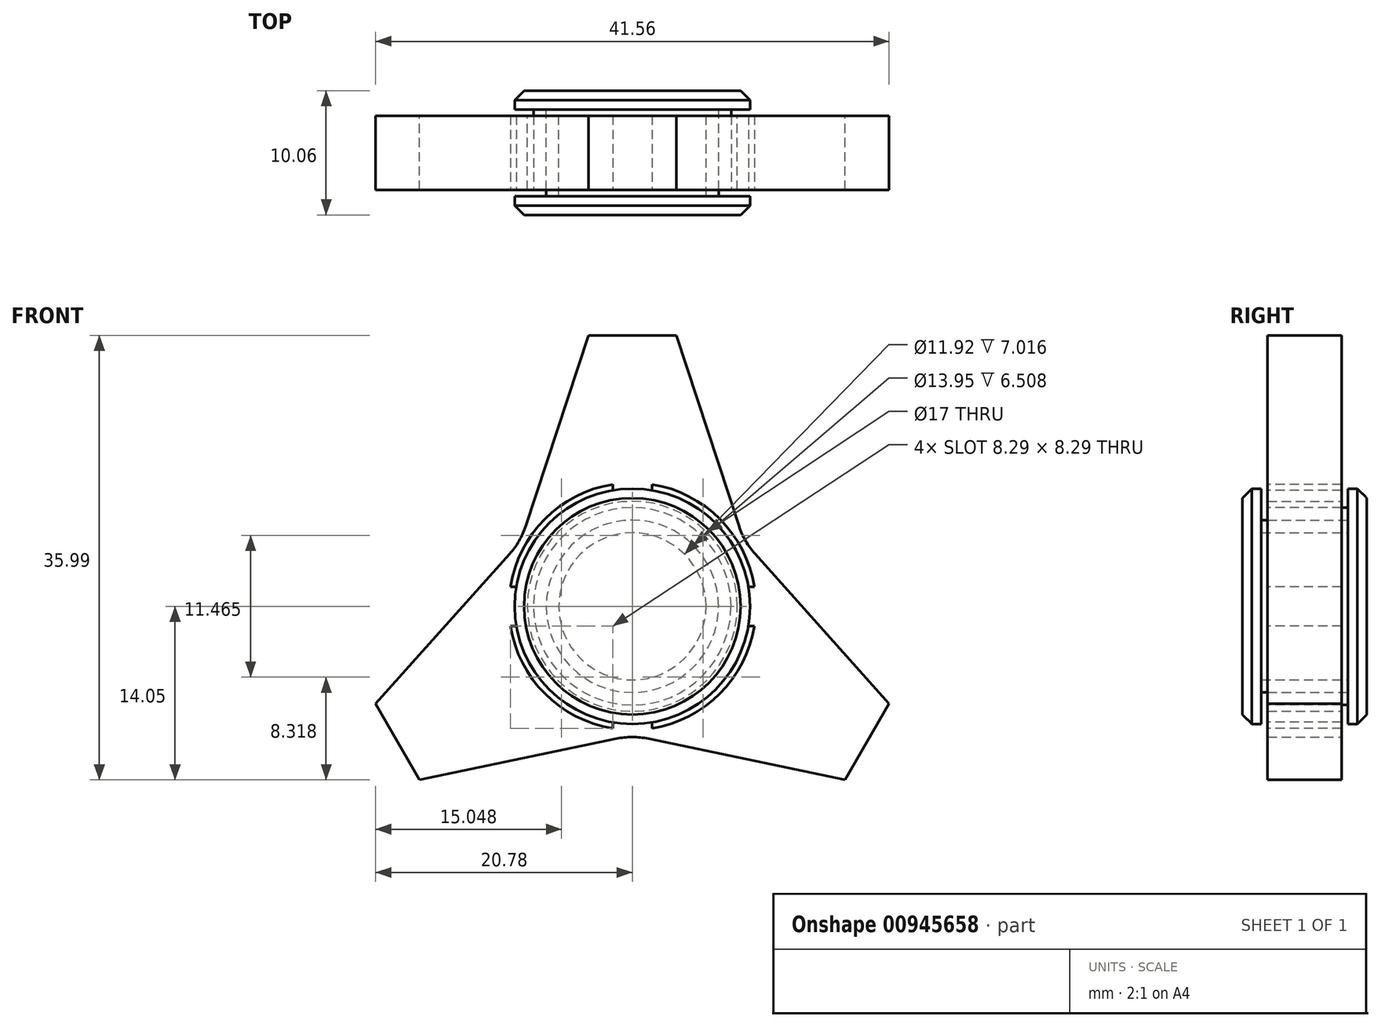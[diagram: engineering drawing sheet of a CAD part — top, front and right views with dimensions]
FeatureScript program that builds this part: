
annotation { "Feature Type Name" : "Feature", "Feature Type Description" : "" }
export const myFeature = defineFeature(function(context is Context, id is Id, definition is map)
    precondition{}
    {
        {
            var Q0;
            Q0=qCreatedBy(makeId("Front.planeOp"),FACE);
            var sketch = newSketch(context, id + "F0", { "sketchPlane" : qUnion([Q0])});
            skCircle(sketch, "E0", {"center": v(0, 0) * mm, "radius": 8.5 * mm});
            skCircle(sketch, "E1.cCircle", {"center": v(0, 0) * mm, "radius": 22.23 * mm, "construction": true});
            skPoint(sketch, "E1.0.midPoint", {"position": v(-19.31, -11) * mm});
            skLineSegment(sketch, "E2", {"start": v(-3.56, 21.94) * mm, "end": v(3.56, 21.94) * mm});
            skLineSegment(sketch, "E3", {"start": v(3.56, 21.94) * mm, "end": v(8.64, 6.49) * mm});
            skLineSegment(sketch, "E4", {"start": v(-3.56, 21.94) * mm, "end": v(-8.64, 6.49) * mm});
            skLineSegment(sketch, "E5.1.0", {"start": v(20.78, -7.89) * mm, "end": v(9.93, 4.24) * mm});
            skLineSegment(sketch, "E5.1.1", {"start": v(17.22, -14.05) * mm, "end": v(1.3, -10.72) * mm});
            skLineSegment(sketch, "E5.1.2", {"start": v(20.78, -7.89) * mm, "end": v(17.22, -14.05) * mm});
            skLineSegment(sketch, "E5.2.0", {"start": v(-17.22, -14.05) * mm, "end": v(-1.3, -10.72) * mm});
            skLineSegment(sketch, "E5.2.1", {"start": v(-20.78, -7.89) * mm, "end": v(-9.93, 4.24) * mm});
            skLineSegment(sketch, "E5.2.2", {"start": v(-17.22, -14.05) * mm, "end": v(-20.78, -7.89) * mm});
            skLineSegment(sketch, "E5.anchor1", {"start": v(0, 0) * mm, "end": v(-10.77, 0) * mm, "construction": true});
            skLineSegment(sketch, "E5.anchor2", {"start": v(0, 0) * mm, "end": v(5.38, -9.33) * mm, "construction": true});
            skPoint(sketch, "E6.orphan", {"position": v(-5.38, 9.33) * mm});
            skPoint(sketch, "E7.orphan", {"position": v(5.38, 9.33) * mm});
            skPoint(sketch, "E8.orphan", {"position": v(-5.38, -9.33) * mm});
            skPoint(sketch, "E9.orphan", {"position": v(10.77, 0) * mm});
            skPoint(sketch, "E10.visualSharp", {"position": v(-9.05, 5.23) * mm});
            skArc(sketch, "E10.filletArc", {"start": v(-9.93, 4.24) * mm, "mid": v(-9.17, 5.3) * mm, "end": v(-8.64, 6.49) * mm});
            skPoint(sketch, "E11.visualSharp", {"position": v(9.05, 5.23) * mm});
            skArc(sketch, "E11.filletArc", {"start": v(8.64, 6.49) * mm, "mid": v(9.17, 5.3) * mm, "end": v(9.93, 4.24) * mm});
            skPoint(sketch, "E12.visualSharp", {"position": v(0, -10.45) * mm});
            skArc(sketch, "E12.filletArc", {"start": v(1.3, -10.72) * mm, "mid": v(0, -10.59) * mm, "end": v(-1.3, -10.72) * mm});
            skSolve(sketch);
        }
        {
            var Q0;
            Q0=makeQuery(id+"F0.imprint","IMPRINT",FACE,{"disambiguationData":[TD([[makeQuery(id+"F0.imprint","IMPRINT",EDGE,{"derivedFrom":sQuery(id+"F0.wireOp",EDGE,"E0")}),-1.0]])]});
            extrude(context, id + "F1", {"entities" : qUnion([Q0]), "depth" : 6 * mm, "offsetDistance" : 25.4 * mm});
        }
        {
            var Q0;
            Q0=makeQuery(id+"F1.opExtrude","CAP_FACE",FACE,{"disambiguationData":[OSD([sQuery(id+"F0.wireOp",EDGE,"E0"),sQuery(id+"F0.wireOp",EDGE,"E2"),sQuery(id+"F0.wireOp",EDGE,"E3"),sQuery(id+"F0.wireOp",EDGE,"E4"),sQuery(id+"F0.wireOp",EDGE,"E5.1.0"),sQuery(id+"F0.wireOp",EDGE,"E5.1.1"),sQuery(id+"F0.wireOp",EDGE,"E5.1.2"),sQuery(id+"F0.wireOp",EDGE,"E5.2.0"),sQuery(id+"F0.wireOp",EDGE,"E5.2.1"),sQuery(id+"F0.wireOp",EDGE,"E5.2.2"),sQuery(id+"F0.wireOp",EDGE,"E10.filletArc"),sQuery(id+"F0.wireOp",EDGE,"E11.filletArc"),sQuery(id+"F0.wireOp",EDGE,"E12.filletArc")])],"isStart":false});
            var sketch = newSketch(context, id + "F2", { "sketchPlane" : qUnion([Q0])});
            skCircle(sketch, "E13.0", {"center": v(0, 0) * mm, "radius": 8 * mm});
            skCircle(sketch, "E14.0", {"center": v(0, 0) * mm, "radius": 6.98 * mm});
            skSolve(sketch);
        }
        {
            var Q0;
            Q0=makeQuery(id+"F2.imprint","IMPRINT",FACE,{"disambiguationData":[TD([[makeQuery(id+"F2.imprint","IMPRINT",EDGE,{"derivedFrom":sQuery(id+"F2.wireOp",EDGE,"E13.0")}),1.0]])]});
            var Q1;
            Q1=makeQuery(id+"F1.opExtrude","CAP_FACE",FACE,{"disambiguationData":[OSD([sQuery(id+"F0.wireOp",EDGE,"E0"),sQuery(id+"F0.wireOp",EDGE,"E2"),sQuery(id+"F0.wireOp",EDGE,"E3"),sQuery(id+"F0.wireOp",EDGE,"E4"),sQuery(id+"F0.wireOp",EDGE,"E5.1.0"),sQuery(id+"F0.wireOp",EDGE,"E5.1.1"),sQuery(id+"F0.wireOp",EDGE,"E5.1.2"),sQuery(id+"F0.wireOp",EDGE,"E5.2.0"),sQuery(id+"F0.wireOp",EDGE,"E5.2.1"),sQuery(id+"F0.wireOp",EDGE,"E5.2.2"),sQuery(id+"F0.wireOp",EDGE,"E10.filletArc"),sQuery(id+"F0.wireOp",EDGE,"E11.filletArc"),sQuery(id+"F0.wireOp",EDGE,"E12.filletArc")])],"isStart":true});
            extrude(context, id + "F3", {"entities" : qUnion([Q0]), "endBound" : BoundingType.UP_TO_SURFACE, "oppositeDirection" : true, "depth" : 25.4 * mm, "endBoundEntityFace" : qUnion([Q1]), "hasOffset" : true, "offsetDistance" : 0.5 * mm, "offsetOppositeDirection" : true});
        }
        {
            var Q0;
            Q0=makeQuery(id+"F3.opExtrude","CAP_FACE",FACE,{"disambiguationData":[OSD([sQuery(id+"F2.wireOp",EDGE,"E13.0"),sQuery(id+"F2.wireOp",EDGE,"E14.0")])],"isStart":false});
            var sketch = newSketch(context, id + "F4", { "sketchPlane" : qUnion([Q0])});
            skCircle(sketch, "E15", {"center": v(0, 0) * mm, "radius": 9.53 * mm});
            skSolve(sketch);
        }
        {
            var Q0;
            Q0=makeQuery(id+"F4.imprint","IMPRINT",FACE,{"disambiguationData":[TD([[makeQuery(id+"F4.imprint","IMPRINT",EDGE,{"derivedFrom":sQuery(id+"F4.wireOp",EDGE,"E15")}),1.0]])]});
            var Q1;
            Q1=makeQuery(id+"F4.imprint","IMPRINT",FACE,{"disambiguationData":[TD([[makeQuery(id+"F4.imprint","IMPRINT",EDGE,{"derivedFrom":makeQuery(id+"F3.opExtrude","CAP_EDGE",EDGE,{"disambiguationData":[OSD([sQuery(id+"F2.wireOp",EDGE,"E14.0")])],"isStart":false})}),1.0]])]});
            var Q2;
            Q2=makeQuery(id+"F4.imprint","IMPRINT",FACE,{"disambiguationData":[TD([[makeQuery(id+"F4.imprint","IMPRINT",EDGE,{"derivedFrom":makeQuery(id+"F3.opExtrude","CAP_EDGE",EDGE,{"disambiguationData":[OSD([sQuery(id+"F2.wireOp",EDGE,"E13.0")])],"isStart":false})}),1.0]])]});
            var Q3;
            Q3=sQuery(id+"F4.wireOp",EDGE,"E15");
            extrude(context, id + "F5", {"entities" : qUnion([Q0, Q1, Q2]), "operationType" : NewBodyOperationType.ADD, "surfaceOperationType" : NewSurfaceOperationType.ADD, "surfaceEntities" : qUnion([Q3]), "depth" : 1.52 * mm, "offsetDistance" : 25.4 * mm});
        }
        {
            var Q0;
            Q0=makeQuery(id+"F5.boolean.opBoolean","SPLIT",FACE,{"disambiguationData":[TD([makeQuery(id+"F3.opExtrude","SWEPT_FACE",FACE,{"disambiguationData":[OSD([sQuery(id+"F2.wireOp",EDGE,"E14.0")])]})])],"derivedFrom":makeQuery(id+"F5.opExtrude","CAP_FACE",FACE,{"disambiguationData":[OSD([sQuery(id+"F4.wireOp",EDGE,"E15")])],"isStart":true})});
            var sketch = newSketch(context, id + "F6", { "sketchPlane" : qUnion([Q0])});
            skCircle(sketch, "E16.0", {"center": v(0, 0) * mm, "radius": 6.98 * mm});
            skCircle(sketch, "E17.0", {"center": v(0, 0) * mm, "radius": 5.96 * mm});
            skSolve(sketch);
        }
        {
            var Q0;
            Q0=makeQuery(id+"F6.imprint","IMPRINT",FACE,{"disambiguationData":[TD([[makeQuery(id+"F6.imprint","IMPRINT",EDGE,{"derivedFrom":sQuery(id+"F6.wireOp",EDGE,"E16.0")}),-1.0]])]});
            var Q1;
            Q1=sQuery(id+"F6.wireOp",EDGE,"E16.0");
            var Q2;
            Q2=makeQuery(id+"F1.opExtrude","CAP_FACE",FACE,{"disambiguationData":[OSD([sQuery(id+"F0.wireOp",EDGE,"E0"),sQuery(id+"F0.wireOp",EDGE,"E2"),sQuery(id+"F0.wireOp",EDGE,"E3"),sQuery(id+"F0.wireOp",EDGE,"E4"),sQuery(id+"F0.wireOp",EDGE,"E5.1.0"),sQuery(id+"F0.wireOp",EDGE,"E5.1.1"),sQuery(id+"F0.wireOp",EDGE,"E5.1.2"),sQuery(id+"F0.wireOp",EDGE,"E5.2.0"),sQuery(id+"F0.wireOp",EDGE,"E5.2.1"),sQuery(id+"F0.wireOp",EDGE,"E5.2.2"),sQuery(id+"F0.wireOp",EDGE,"E10.filletArc"),sQuery(id+"F0.wireOp",EDGE,"E11.filletArc"),sQuery(id+"F0.wireOp",EDGE,"E12.filletArc")])],"isStart":false});
            extrude(context, id + "F7", {"entities" : qUnion([Q0]), "surfaceEntities" : qUnion([Q1]), "endBound" : BoundingType.UP_TO_SURFACE, "depth" : 25.4 * mm, "endBoundEntityFace" : qUnion([Q2]), "hasOffset" : true, "offsetDistance" : 0.5 * mm, "offsetOppositeDirection" : true});
        }
        {
            var Q0;
            Q0=makeQuery(id+"F7.opExtrude","CAP_FACE",FACE,{"disambiguationData":[OSD([sQuery(id+"F6.wireOp",EDGE,"E16.0"),sQuery(id+"F6.wireOp",EDGE,"E17.0")])],"isStart":false});
            var sketch = newSketch(context, id + "F8", { "sketchPlane" : qUnion([Q0])});
            skCircle(sketch, "E18.0", {"center": v(0, 0) * mm, "radius": 9.53 * mm});
            skSolve(sketch);
        }
        {
            var Q0;
            Q0=makeQuery(id+"F8.imprint","IMPRINT",FACE,{"disambiguationData":[TD([[makeQuery(id+"F8.imprint","IMPRINT",EDGE,{"derivedFrom":sQuery(id+"F8.wireOp",EDGE,"E18.0")}),1.0]])]});
            var Q1;
            Q1=makeQuery(id+"F8.imprint","IMPRINT",FACE,{"disambiguationData":[TD([[makeQuery(id+"F8.imprint","IMPRINT",EDGE,{"derivedFrom":makeQuery(id+"F7.opExtrude","CAP_EDGE",EDGE,{"disambiguationData":[OSD([sQuery(id+"F6.wireOp",EDGE,"E16.0")])],"isStart":false})}),-1.0]])]});
            var Q2;
            Q2=makeQuery(id+"F8.imprint","IMPRINT",FACE,{"disambiguationData":[TD([[makeQuery(id+"F8.imprint","IMPRINT",EDGE,{"derivedFrom":makeQuery(id+"F7.opExtrude","CAP_EDGE",EDGE,{"disambiguationData":[OSD([sQuery(id+"F6.wireOp",EDGE,"E17.0")])],"isStart":false})}),1.0]])]});
            extrude(context, id + "F9", {"entities" : qUnion([Q0, Q1, Q2]), "operationType" : NewBodyOperationType.ADD, "depth" : 1.52 * mm, "offsetDistance" : 25.4 * mm});
        }
        {
            var Q0;
            Q0=makeQuery(id+"F5.opExtrude","CAP_EDGE",EDGE,{"disambiguationData":[OSD([sQuery(id+"F4.wireOp",EDGE,"E15")])],"isStart":false});
            var Q1;
            Q1=makeQuery(id+"F9.opExtrude","CAP_EDGE",EDGE,{"disambiguationData":[OSD([sQuery(id+"F8.wireOp",EDGE,"E18.0")])],"isStart":false});
            chamfer(context, id + "F10", {"entities" : qUnion([Q0, Q1]), "width" : 0.76 * mm, "tangentPropagation" : true});
        }
        {
            var Q0;
            Q0=makeQuery(id+"F1.opExtrude","CAP_FACE",FACE,{"disambiguationData":[OSD([sQuery(id+"F0.wireOp",EDGE,"E0"),sQuery(id+"F0.wireOp",EDGE,"E2"),sQuery(id+"F0.wireOp",EDGE,"E3"),sQuery(id+"F0.wireOp",EDGE,"E4"),sQuery(id+"F0.wireOp",EDGE,"E5.1.0"),sQuery(id+"F0.wireOp",EDGE,"E5.1.1"),sQuery(id+"F0.wireOp",EDGE,"E5.1.2"),sQuery(id+"F0.wireOp",EDGE,"E5.2.0"),sQuery(id+"F0.wireOp",EDGE,"E5.2.1"),sQuery(id+"F0.wireOp",EDGE,"E5.2.2"),sQuery(id+"F0.wireOp",EDGE,"E10.filletArc"),sQuery(id+"F0.wireOp",EDGE,"E11.filletArc"),sQuery(id+"F0.wireOp",EDGE,"E12.filletArc")])],"isStart":false});
            var sketch = newSketch(context, id + "F11", { "sketchPlane" : qUnion([Q0])});
            skCircle(sketch, "E19.cCircle", {"center": v(0, 35.56) * mm, "radius": 5.49 * mm, "construction": true});
            skLineSegment(sketch, "E19.0", {"start": v(5.49, 32.4) * mm, "end": v(0, 29.22) * mm});
            skLineSegment(sketch, "E19.1", {"start": v(0, 29.22) * mm, "end": v(-5.49, 32.4) * mm});
            skLineSegment(sketch, "E19.2", {"start": v(-5.49, 32.4) * mm, "end": v(-5.49, 38.73) * mm});
            skLineSegment(sketch, "E19.3", {"start": v(-5.49, 38.73) * mm, "end": v(0, 41.9) * mm});
            skLineSegment(sketch, "E19.4", {"start": v(0, 41.9) * mm, "end": v(5.49, 38.73) * mm});
            skLineSegment(sketch, "E19.5", {"start": v(5.49, 38.73) * mm, "end": v(5.49, 32.4) * mm});
            skPoint(sketch, "E19.0.midPoint", {"position": v(2.74, 30.8) * mm});
            skSolve(sketch);
        }
        {
            var Q0;
            Q0=makeQuery(id+"F11.imprint","IMPRINT",FACE,{"disambiguationData":[TD([[makeQuery(id+"F11.imprint","IMPRINT",EDGE,{"derivedFrom":sQuery(id+"F11.wireOp",EDGE,"E19.0")}),-1.0]])]});
            extrude(context, id + "F12", {"entities" : qUnion([Q0]), "operationType" : NewBodyOperationType.REMOVE, "endBound" : BoundingType.THROUGH_ALL, "oppositeDirection" : true, "depth" : 25.4 * mm, "offsetDistance" : 25.4 * mm});
        }
        {
            var Q0;
            Q0=makeQuery(id+"F1.opExtrude","CAP_FACE",FACE,{"disambiguationData":[OSD([sQuery(id+"F0.wireOp",EDGE,"E0"),sQuery(id+"F0.wireOp",EDGE,"E2"),sQuery(id+"F0.wireOp",EDGE,"E3"),sQuery(id+"F0.wireOp",EDGE,"E4"),sQuery(id+"F0.wireOp",EDGE,"E5.1.0"),sQuery(id+"F0.wireOp",EDGE,"E5.1.1"),sQuery(id+"F0.wireOp",EDGE,"E5.1.2"),sQuery(id+"F0.wireOp",EDGE,"E5.2.0"),sQuery(id+"F0.wireOp",EDGE,"E5.2.1"),sQuery(id+"F0.wireOp",EDGE,"E5.2.2"),sQuery(id+"F0.wireOp",EDGE,"E10.filletArc"),sQuery(id+"F0.wireOp",EDGE,"E11.filletArc"),sQuery(id+"F0.wireOp",EDGE,"E12.filletArc")])],"isStart":false});
            var sketch = newSketch(context, id + "F13", { "sketchPlane" : qUnion([Q0])});
            skArc(sketch, "E20", {"start": v(-1.59, 9.88) * mm, "mid": v(-7.07, 7.07) * mm, "end": v(-9.88, 1.59) * mm});
            skArc(sketch, "E21.trimOffspring", {"start": v(1.59, -9.88) * mm, "mid": v(7.07, -7.07) * mm, "end": v(9.88, -1.59) * mm});
            skPoint(sketch, "E22.orphan", {"position": v(0.39, -10) * mm});
            skArc(sketch, "E23.trimOffspring", {"start": v(9.88, 1.59) * mm, "mid": v(7.07, 7.07) * mm, "end": v(1.59, 9.88) * mm});
            skArc(sketch, "E24.trimOffspring", {"start": v(-9.88, -1.59) * mm, "mid": v(-7.07, -7.07) * mm, "end": v(-1.59, -9.88) * mm});
            skLineSegment(sketch, "E25", {"start": v(-1.59, 9.88) * mm, "end": v(-1.59, 9.4) * mm});
            skLineSegment(sketch, "E26", {"start": v(1.59, 9.4) * mm, "end": v(1.59, 9.88) * mm});
            skLineSegment(sketch, "E27", {"start": v(-9.88, 1.59) * mm, "end": v(-9.38, 1.59) * mm});
            skLineSegment(sketch, "E28", {"start": v(-9.88, -1.59) * mm, "end": v(-9.4, -1.59) * mm});
            skLineSegment(sketch, "E29", {"start": v(9.88, 1.59) * mm, "end": v(9.38, 1.59) * mm});
            skLineSegment(sketch, "E30", {"start": v(9.88, -1.59) * mm, "end": v(9.39, -1.59) * mm});
            skLineSegment(sketch, "E31", {"start": v(-1.59, -9.88) * mm, "end": v(-1.59, -9.4) * mm});
            skLineSegment(sketch, "E32", {"start": v(1.59, -9.88) * mm, "end": v(1.59, -9.4) * mm});
            skArc(sketch, "E33", {"start": v(1.59, -9.4) * mm, "mid": v(6.74, -6.74) * mm, "end": v(9.4, -1.59) * mm});
            skArc(sketch, "E34.trimOffspring", {"start": v(-9.4, -1.59) * mm, "mid": v(-6.74, -6.74) * mm, "end": v(-1.59, -9.4) * mm});
            skArc(sketch, "E35.trimOffspring", {"start": v(9.4, 1.59) * mm, "mid": v(6.74, 6.74) * mm, "end": v(1.59, 9.4) * mm});
            skArc(sketch, "E36.trimOffspring", {"start": v(-1.59, 9.4) * mm, "mid": v(-6.74, 6.74) * mm, "end": v(-9.4, 1.59) * mm});
            skPoint(sketch, "E37.orphan", {"position": v(1.59, 9.15) * mm});
            skSolve(sketch);
        }
        {
            var Q0;
            {var subQ0=sQuery(id+"F13.wireOp",EDGE,"E20");Q0=makeQuery(id+"F13.imprint","IMPRINT",FACE,{"disambiguationData":[TD([[makeQuery(id+"F13.imprint","IMPRINT",EDGE,{"derivedFrom":subQ0}),1.0]])]});}
            var Q1;
            {var subQ0=sQuery(id+"F13.wireOp",EDGE,"E23.trimOffspring");Q1=makeQuery(id+"F13.imprint","IMPRINT",FACE,{"disambiguationData":[TD([[makeQuery(id+"F13.imprint","IMPRINT",EDGE,{"derivedFrom":subQ0}),1.0]])]});}
            var Q2;
            {var subQ0=sQuery(id+"F13.wireOp",EDGE,"E24.trimOffspring");Q2=makeQuery(id+"F13.imprint","IMPRINT",FACE,{"disambiguationData":[TD([[makeQuery(id+"F13.imprint","IMPRINT",EDGE,{"derivedFrom":subQ0}),1.0]])]});}
            var Q3;
            {var subQ0=sQuery(id+"F13.wireOp",EDGE,"E21.trimOffspring");Q3=makeQuery(id+"F13.imprint","IMPRINT",FACE,{"disambiguationData":[TD([[makeQuery(id+"F13.imprint","IMPRINT",EDGE,{"derivedFrom":subQ0}),1.0]])]});}
            extrude(context, id + "F14", {"entities" : qUnion([Q0, Q1, Q2, Q3]), "operationType" : NewBodyOperationType.REMOVE, "endBound" : BoundingType.THROUGH_ALL, "oppositeDirection" : true, "depth" : 5.08 * mm, "offsetDistance" : 25.4 * mm});
        }
    });
